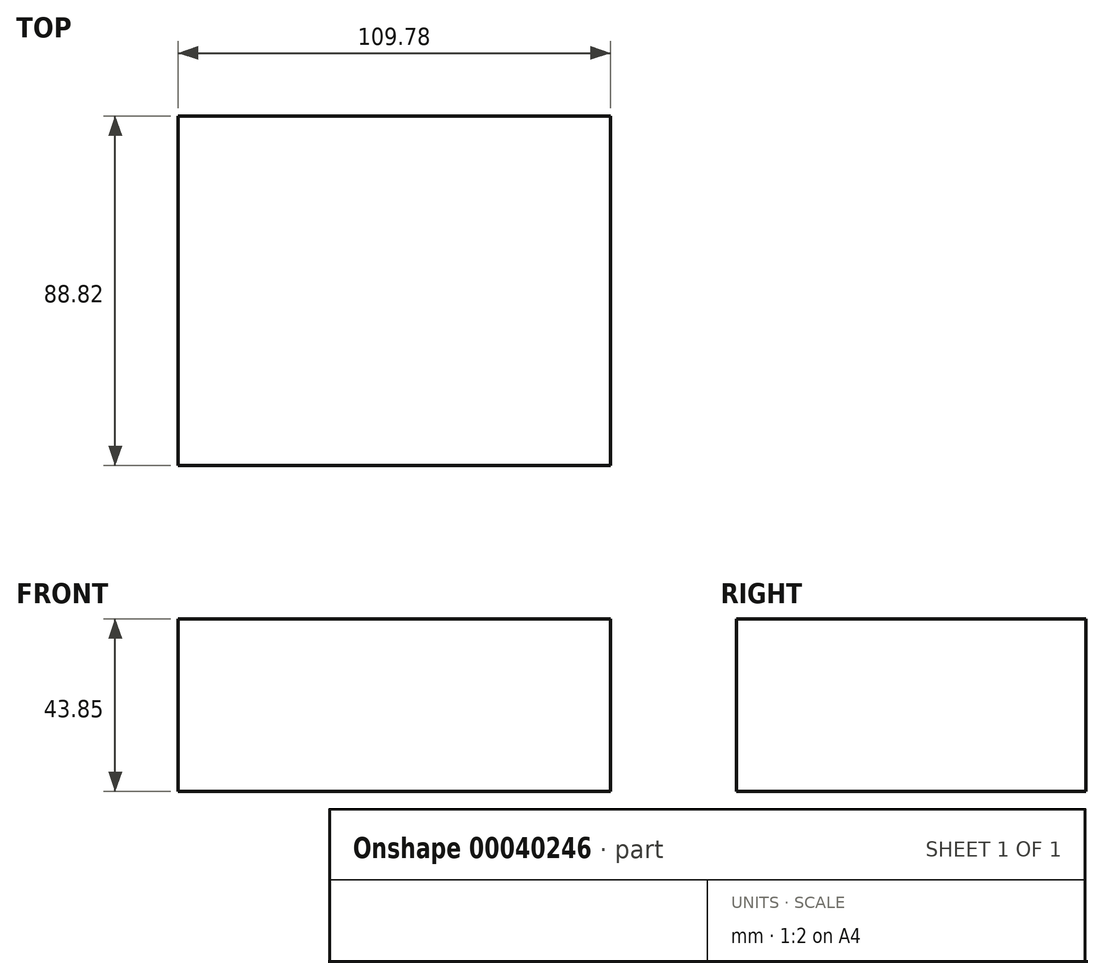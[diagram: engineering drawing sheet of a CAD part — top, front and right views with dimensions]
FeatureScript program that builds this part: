
annotation { "Feature Type Name" : "Feature", "Feature Type Description" : "" }
export const myFeature = defineFeature(function(context is Context, id is Id, definition is map)
    precondition{}
    {
        {
            var Q0;
            Q0=qCreatedBy(makeId("Top.planeOp"),FACE);
            var sketch = newSketch(context, id + "F0", { "sketchPlane" : qUnion([Q0])});
            skLineSegment(sketch, "E0.bottom", {"start": v(-57.15, 57.39) * mm, "end": v(52.63, 57.39) * mm});
            skLineSegment(sketch, "E0.top", {"start": v(-57.15, -31.43) * mm, "end": v(52.63, -31.43) * mm});
            skLineSegment(sketch, "E0.left", {"start": v(-57.15, 57.39) * mm, "end": v(-57.15, -31.43) * mm});
            skLineSegment(sketch, "E0.right", {"start": v(52.63, 57.39) * mm, "end": v(52.63, -31.43) * mm});
            skSolve(sketch);
        }
        {
            var Q0;
            Q0=makeQuery(id+"F0.imprint","IMPRINT",FACE,{"disambiguationData":[TD([[makeQuery(id+"F0.imprint","IMPRINT",EDGE,{"derivedFrom":sQuery(id+"F0.wireOp",EDGE,"E0.bottom")}),-1.0]])]});
            extrude(context, id + "F1", {"entities" : qUnion([Q0]), "depth" : 43.85 * mm});
        }
    });
